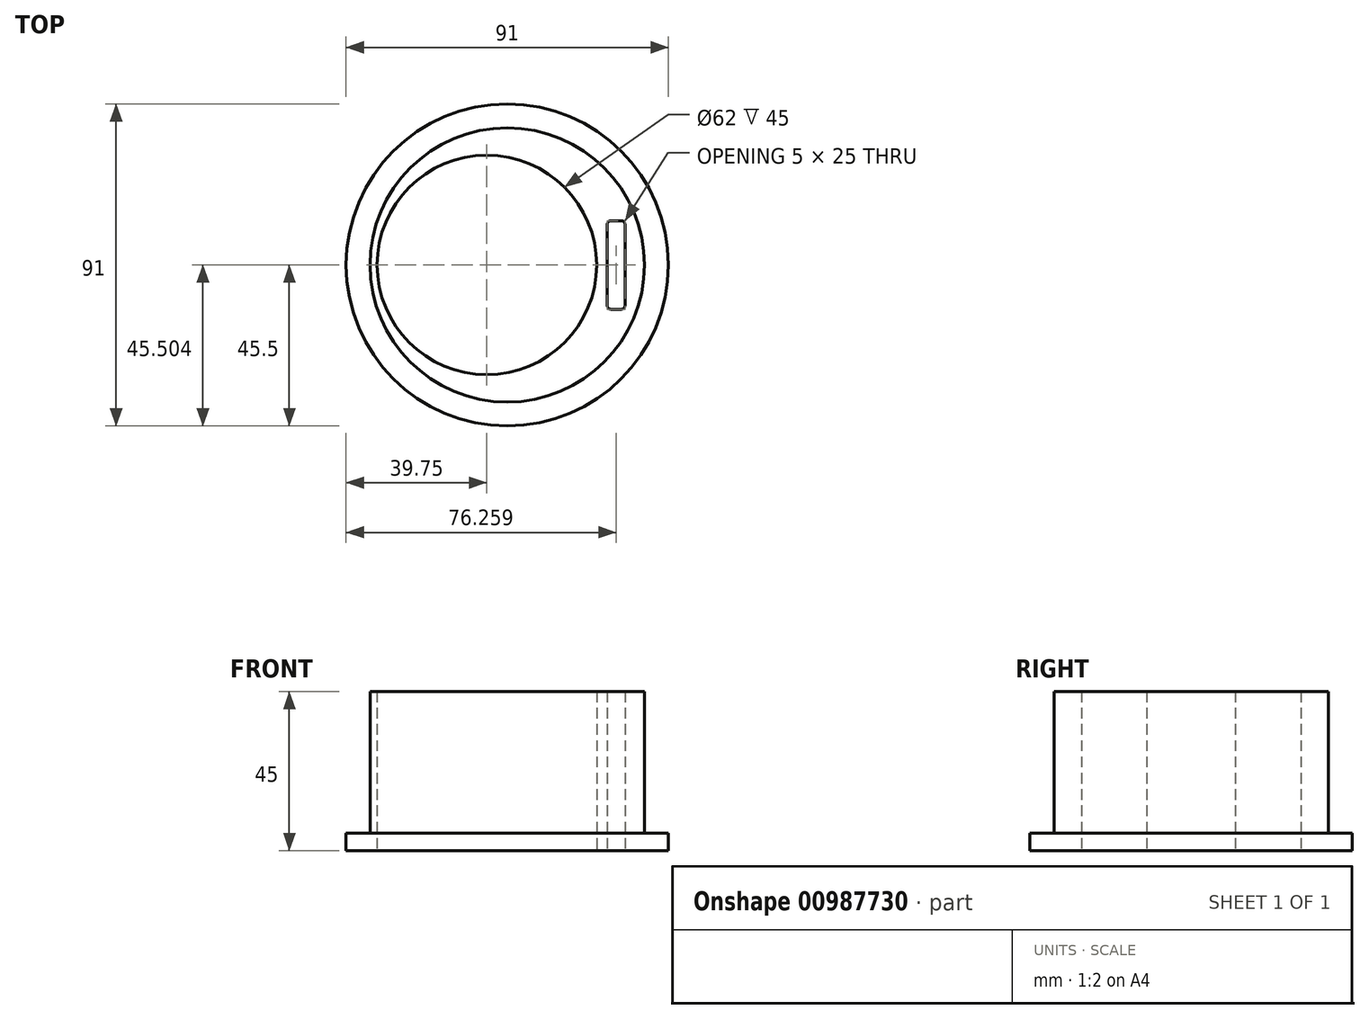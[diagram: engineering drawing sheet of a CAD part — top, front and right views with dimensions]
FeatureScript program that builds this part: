
annotation { "Feature Type Name" : "Feature", "Feature Type Description" : "" }
export const myFeature = defineFeature(function(context is Context, id is Id, definition is map)
    precondition{}
    {
        {
            var Q0;
            Q0=qCreatedBy(makeId("Top.planeOp"),FACE);
            var sketch = newSketch(context, id + "F0", { "sketchPlane" : qUnion([Q0])});
            skCircle(sketch, "E0", {"center": v(0, 0) * mm, "radius": 38.75 * mm});
            skCircle(sketch, "E1", {"center": v(-5.75, 0) * mm, "radius": 31 * mm});
            skLineSegment(sketch, "E2.bottom", {"start": v(32.26, -12.5) * mm, "end": v(29.26, -12.5) * mm});
            skLineSegment(sketch, "E2.top", {"start": v(32.26, 12.5) * mm, "end": v(29.26, 12.5) * mm});
            skLineSegment(sketch, "E2.left", {"start": v(33.26, -11.5) * mm, "end": v(33.26, 11.5) * mm});
            skLineSegment(sketch, "E2.right", {"start": v(28.26, -11.5) * mm, "end": v(28.26, 11.5) * mm});
            skPoint(sketch, "E2.middle", {"position": v(30.76, 0) * mm});
            skPoint(sketch, "E3.visualSharp", {"position": v(28.26, 12.5) * mm});
            skArc(sketch, "E3.filletArc", {"start": v(29.26, 12.5) * mm, "mid": v(28.55, 12.2) * mm, "end": v(28.26, 11.5) * mm});
            skPoint(sketch, "E4.visualSharp", {"position": v(33.26, 12.5) * mm});
            skArc(sketch, "E4.filletArc", {"start": v(33.26, 11.5) * mm, "mid": v(32.97, 12.2) * mm, "end": v(32.26, 12.5) * mm});
            skPoint(sketch, "E5.visualSharp", {"position": v(33.26, -12.5) * mm});
            skArc(sketch, "E5.filletArc", {"start": v(32.26, -12.5) * mm, "mid": v(32.97, -12.2) * mm, "end": v(33.26, -11.5) * mm});
            skPoint(sketch, "E6.visualSharp", {"position": v(28.26, -12.5) * mm});
            skArc(sketch, "E6.filletArc", {"start": v(28.26, -11.5) * mm, "mid": v(28.55, -12.2) * mm, "end": v(29.26, -12.5) * mm});
            skCircle(sketch, "E7", {"center": v(0, 0) * mm, "radius": 45.5 * mm});
            skSolve(sketch);
        }
        {
            var Q0;
            Q0=makeQuery(id+"F0.imprint","IMPRINT",FACE,{"disambiguationData":[TD([[makeQuery(id+"F0.imprint","IMPRINT",EDGE,{"derivedFrom":sQuery(id+"F0.wireOp",EDGE,"E0")}),-1.0]])]});
            extrude(context, id + "F1", {"entities" : qUnion([Q0]), "depth" : 5 * mm, "offsetDistance" : 25 * mm});
        }
        {
            var Q0;
            Q0=makeQuery(id+"F0.imprint","IMPRINT",FACE,{"disambiguationData":[TD([[makeQuery(id+"F0.imprint","IMPRINT",EDGE,{"derivedFrom":sQuery(id+"F0.wireOp",EDGE,"E0")}),1.0]])]});
            extrude(context, id + "F2", {"entities" : qUnion([Q0]), "operationType" : NewBodyOperationType.ADD, "depth" : 45 * mm, "offsetDistance" : 25 * mm});
        }
    });
